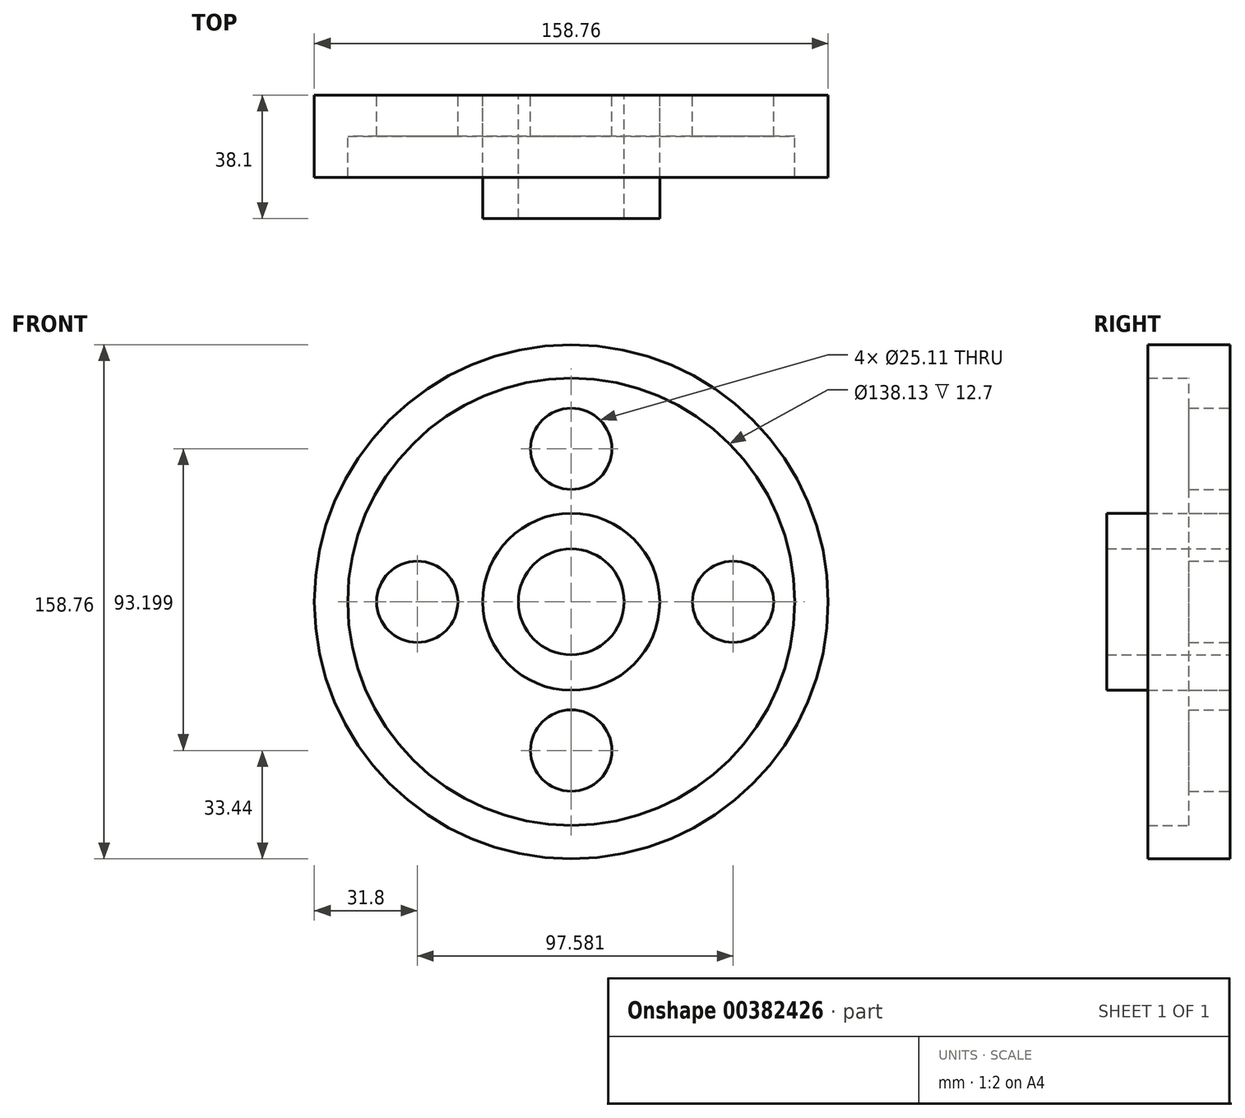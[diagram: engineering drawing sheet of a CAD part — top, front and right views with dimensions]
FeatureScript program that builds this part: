
annotation { "Feature Type Name" : "Feature", "Feature Type Description" : "" }
export const myFeature = defineFeature(function(context is Context, id is Id, definition is map)
    precondition{}
    {
        {
            var Q0;
            Q0=qCreatedBy(makeId("Front.planeOp"),FACE);
            var sketch = newSketch(context, id + "F0", { "sketchPlane" : qUnion([Q0])});
            skCircle(sketch, "E0", {"center": v(0, 0) * mm, "radius": 69.07 * mm});
            skCircle(sketch, "E1", {"center": v(0, 0) * mm, "radius": 27.34 * mm});
            skCircle(sketch, "E2", {"center": v(0, 0) * mm, "radius": 16.34 * mm});
            skCircle(sketch, "E3", {"center": v(0, 0) * mm, "radius": 79.38 * mm});
            skCircle(sketch, "E4", {"center": v(50, 0) * mm, "radius": 12.55 * mm});
            skCircle(sketch, "E5", {"center": v(-47.58, 0) * mm, "radius": 12.55 * mm});
            skCircle(sketch, "E6", {"center": v(0, 47.26) * mm, "radius": 12.55 * mm});
            skCircle(sketch, "E7", {"center": v(0, -45.94) * mm, "radius": 12.55 * mm});
            skSolve(sketch);
        }
        {
            var Q0;
            Q0=makeQuery(id+"F0.imprint","IMPRINT",FACE,{"disambiguationData":[TD([[makeQuery(id+"F0.imprint","IMPRINT",EDGE,{"derivedFrom":sQuery(id+"F0.wireOp",EDGE,"E1")}),1.0]])]});
            extrude(context, id + "F1", {"entities" : qUnion([Q0]), "depth" : 38.1 * mm});
        }
        {
            var Q0;
            Q0=makeQuery(id+"F0.imprint","IMPRINT",FACE,{"disambiguationData":[TD([[makeQuery(id+"F0.imprint","IMPRINT",EDGE,{"derivedFrom":sQuery(id+"F0.wireOp",EDGE,"E0")}),1.0]])]});
            extrude(context, id + "F2", {"entities" : qUnion([Q0]), "depth" : 12.7 * mm});
        }
        {
            var Q0;
            Q0=makeQuery(id+"F0.imprint","IMPRINT",FACE,{"disambiguationData":[TD([[makeQuery(id+"F0.imprint","IMPRINT",EDGE,{"derivedFrom":sQuery(id+"F0.wireOp",EDGE,"E0")}),-1.0]])]});
            extrude(context, id + "F3", {"entities" : qUnion([Q0]), "operationType" : NewBodyOperationType.ADD, "depth" : 25.4 * mm});
        }
    });
